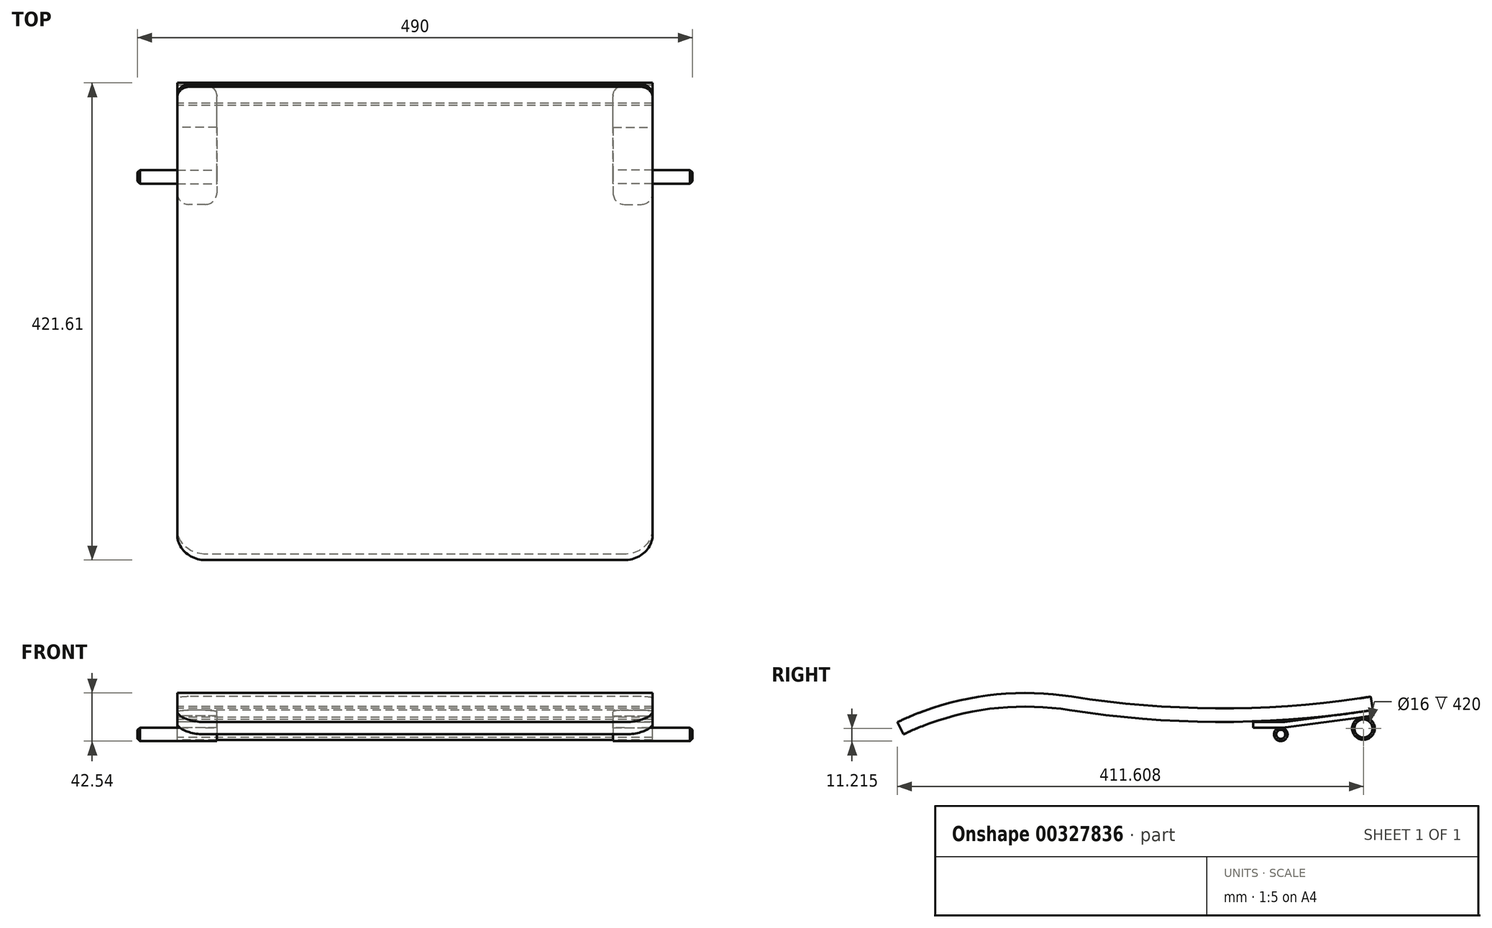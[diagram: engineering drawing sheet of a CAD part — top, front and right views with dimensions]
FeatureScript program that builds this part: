
annotation { "Feature Type Name" : "Feature", "Feature Type Description" : "" }
export const myFeature = defineFeature(function(context is Context, id is Id, definition is map)
    precondition{}
    {
        {
            var Q0;
            Q0=qCreatedBy(makeId("Right.planeOp"),FACE);
            var sketch = newSketch(context, id + "F0", { "sketchPlane" : qUnion([Q0])});
            skArc(sketch, "E0", {"start": v(-227.52, 21.5) * mm, "mid": v(-302.58, 21.9) * mm, "end": v(-374.38, 0) * mm});
            skArc(sketch, "E1", {"start": v(-227.52, 21.5) * mm, "mid": v(-93.54, 11.02) * mm, "end": v(40.43, 21.5) * mm});
            skArc(sketch, "E2.0", {"start": v(-225.65, 33.35) * mm, "mid": v(-304.32, 33.77) * mm, "end": v(-379.57, 10.82) * mm});
            skArc(sketch, "E2.1", {"start": v(-225.65, 33.35) * mm, "mid": v(-93.54, 23.02) * mm, "end": v(38.57, 33.35) * mm});
            skLineSegment(sketch, "E3", {"start": v(-379.57, 10.82) * mm, "end": v(-374.38, 0) * mm});
            skLineSegment(sketch, "E4", {"start": v(40.43, 21.5) * mm, "end": v(38.57, 33.35) * mm});
            skLineSegment(sketch, "E5", {"start": v(38.57, 33.35) * mm, "end": v(38.57, 33.35) * mm});
            skLineSegment(sketch, "E6", {"start": v(40.43, 21.5) * mm, "end": v(40.43, 21.5) * mm});
            skSolve(sketch);
        }
        {
            var Q0;
            Q0 = qSketchRegion(id + "F0", true);
            extrude(context, id + "F1", {"entities" : qUnion([Q0]), "endBound" : BoundingType.SYMMETRIC, "depth" : 420 * mm});
        }
        {
            var Q0;
            Q0=qCreatedBy(makeId("Right.planeOp"),FACE);
            var sketch = newSketch(context, id + "F2", { "sketchPlane" : qUnion([Q0])});
            skArc(sketch, "E7.0", {"start": v(-227.52, 21.5) * mm, "mid": v(-93.54, 11.02) * mm, "end": v(40.43, 21.5) * mm});
            skLineSegment(sketch, "E8", {"start": v(-65.33, 11) * mm, "end": v(-65.33, 6) * mm});
            skLineSegment(sketch, "E9", {"start": v(-65.33, 6) * mm, "end": v(-37.7, 6) * mm});
            skLineSegment(sketch, "E10", {"start": v(-36.77, 6.06) * mm, "end": v(40.62, 16.46) * mm});
            skLineSegment(sketch, "E11", {"start": v(40.62, 16.46) * mm, "end": v(39.95, 21.41) * mm});
            skLineSegment(sketch, "E12.0", {"start": v(-37.43, 11.02) * mm, "end": v(39.95, 21.41) * mm});
            skLineSegment(sketch, "E12.1", {"start": v(-65.33, 11) * mm, "end": v(-37.7, 11) * mm});
            skCircle(sketch, "E13", {"center": v(-40.94, 0) * mm, "radius": 6 * mm});
            skPoint(sketch, "E14.visualSharp", {"position": v(-37.57, 11) * mm});
            skArc(sketch, "E14.filletArc", {"start": v(-37.7, 11) * mm, "mid": v(-37.57, 11) * mm, "end": v(-37.43, 11.02) * mm});
            skPoint(sketch, "E15.visualSharp", {"position": v(-37.23, 6) * mm});
            skArc(sketch, "E15.filletArc", {"start": v(-37.7, 6) * mm, "mid": v(-37.23, 6.02) * mm, "end": v(-36.77, 6.06) * mm});
            skSolve(sketch);
        }
        {
            var Q0;
            Q0=makeQuery(id+"F1.opExtrude","CAP_EDGE",EDGE,{"disambiguationData":[OSD([sQuery(id+"F0.wireOp",EDGE,"E3")])],"isStart":false});
            var Q1;
            Q1=makeQuery(id+"F1.opExtrude","CAP_EDGE",EDGE,{"disambiguationData":[OSD([sQuery(id+"F0.wireOp",EDGE,"E3")])],"isStart":true});
            fillet(context, id + "F3", {"entities" : qUnion([Q0, Q1]), "radius" : 25 * mm, "tangentPropagation" : true, "allowEdgeOverflow" : false});
        }
        {
            var Q0;
            Q0=makeQuery(id+"F1.opExtrude","CAP_EDGE",EDGE,{"disambiguationData":[OSD([sQuery(id+"F0.wireOp",EDGE,"E4")])],"isStart":false});
            var Q1;
            Q1=makeQuery(id+"F1.opExtrude","CAP_EDGE",EDGE,{"disambiguationData":[OSD([sQuery(id+"F0.wireOp",EDGE,"E4")])],"isStart":true});
            fillet(context, id + "F4", {"entities" : qUnion([Q0, Q1]), "radius" : 10 * mm, "tangentPropagation" : true, "allowEdgeOverflow" : false});
        }
        {
            var Q0;
            Q0=qCreatedBy(makeId("Right.planeOp"),FACE);
            var sketch = newSketch(context, id + "F5", { "sketchPlane" : qUnion([Q0])});
            skCircle(sketch, "E16", {"center": v(32.04, 5.22) * mm, "radius": 10 * mm});
            skCircle(sketch, "E17", {"center": v(32.04, 5.22) * mm, "radius": 8 * mm});
            skSolve(sketch);
        }
        {
            var Q0;
            Q0=makeQuery(id+"F5.imprint","IMPRINT",FACE,{"disambiguationData":[TD([[makeQuery(id+"F5.imprint","IMPRINT",EDGE,{"derivedFrom":sQuery(id+"F5.wireOp",EDGE,"E16")}),1.0]])]});
            var Q1;
            Q1=makeQuery(id+"FTDRgdQHSnS7fxQ_1.opExtrude","CAP_FACE",FACE,{"disambiguationData":[OSD([sQuery(id+"FFSUCwoas4lt323_1.wireOp",EDGE,"86147a53-e2fd-4186-82ed-e5d5ec7286ad.0.0"),sQuery(id+"FFSUCwoas4lt323_1.wireOp",EDGE,"86147a53-e2fd-4186-82ed-e5d5ec7286ad.0.1"),sQuery(id+"FFSUCwoas4lt323_1.wireOp",EDGE,"86147a53-e2fd-4186-82ed-e5d5ec7286ad.0.2"),sQuery(id+"FFSUCwoas4lt323_1.wireOp",EDGE,"86147a53-e2fd-4186-82ed-e5d5ec7286ad.0.3"),sQuery(id+"FFSUCwoas4lt323_1.wireOp",EDGE,"86147a53-e2fd-4186-82ed-e5d5ec7286ad.0.4"),sQuery(id+"FFSUCwoas4lt323_1.wireOp",EDGE,"86147a53-e2fd-4186-82ed-e5d5ec7286ad.0.5"),sQuery(id+"FFSUCwoas4lt323_1.wireOp",EDGE,"86147a53-e2fd-4186-82ed-e5d5ec7286ad.0.6")])],"isStart":true});
            extrude(context, id + "F6", {"entities" : qUnion([Q0]), "endBound" : BoundingType.SYMMETRIC, "depth" : 420 * mm, "hasSecondDirection" : true, "secondDirectionBound" : SecondDirectionBoundingType.UP_TO_SURFACE, "secondDirectionOppositeDirection" : true, "secondDirectionBoundEntityFace" : qUnion([Q1]), "secondDirectionDepth" : 25 * mm});
        }
        {
            var Q0;
            Q0=makeQuery(id+"F1.opExtrude","CAP_FACE",FACE,{"disambiguationData":[OSD([sQuery(id+"F0.wireOp",EDGE,"E0"),sQuery(id+"F0.wireOp",EDGE,"E1"),sQuery(id+"F0.wireOp",EDGE,"E2.0"),sQuery(id+"F0.wireOp",EDGE,"E2.1"),sQuery(id+"F0.wireOp",EDGE,"E3"),sQuery(id+"F0.wireOp",EDGE,"E4")])],"isStart":false});
            var sketch = newSketch(context, id + "F7", { "sketchPlane" : qUnion([Q0])});
            skLineSegment(sketch, "E18.0.0", {"start": v(39.95, 21.41) * mm, "end": v(39.53, 21.36) * mm});
            skArc(sketch, "E18.0.1", {"start": v(39.53, 21.36) * mm, "mid": v(21.22, 18.7) * mm, "end": v(2.86, 16.43) * mm});
            skLineSegment(sketch, "E18.0.2", {"start": v(2.86, 16.43) * mm, "end": v(-37.43, 11.02) * mm});
            skArc(sketch, "E18.0.3", {"start": v(-37.43, 11.02) * mm, "mid": v(-37.57, 11) * mm, "end": v(-37.7, 11) * mm});
            skLineSegment(sketch, "E18.0.4", {"start": v(-37.7, 11) * mm, "end": v(-65.33, 11) * mm});
            skLineSegment(sketch, "E18.0.5", {"start": v(-65.33, 11) * mm, "end": v(-65.33, 6) * mm});
            skLineSegment(sketch, "E18.0.6", {"start": v(-65.33, 6) * mm, "end": v(-40.94, 6) * mm});
            skLineSegment(sketch, "E18.0.7", {"start": v(-40.94, 6) * mm, "end": v(-37.7, 6) * mm});
            skArc(sketch, "E18.0.8", {"start": v(-37.7, 6) * mm, "mid": v(-37.23, 6.02) * mm, "end": v(-36.77, 6.06) * mm});
            skLineSegment(sketch, "E18.0.9", {"start": v(-36.77, 6.06) * mm, "end": v(40.62, 16.46) * mm});
            skLineSegment(sketch, "E18.0.10", {"start": v(40.62, 16.46) * mm, "end": v(39.95, 21.41) * mm});
            skCircle(sketch, "E18.1.0", {"center": v(-40.94, 0) * mm, "radius": 6 * mm});
            skSolve(sketch);
        }
        {
            var Q0;
            {var subQ0=sQuery(id+"F7.wireOp",EDGE,"E18.0.0");Q0=makeQuery(id+"F7.imprint","IMPRINT",FACE,{"disambiguationData":[TD([[makeQuery(id+"F7.imprint","IMPRINT",EDGE,{"derivedFrom":subQ0}),1.0]])]});}
            extrude(context, id + "F8", {"entities" : qUnion([Q0]), "oppositeDirection" : true, "depth" : 35 * mm});
        }
        {
            var Q0;
            Q0=makeQuery(id+"F8.opExtrude","CAP_EDGE",EDGE,{"disambiguationData":[OSD([sQuery(id+"F7.wireOp",EDGE,"E18.0.5")])],"isStart":true});
            var Q1;
            Q1=makeQuery(id+"F8.opExtrude","CAP_EDGE",EDGE,{"disambiguationData":[OSD([sQuery(id+"F7.wireOp",EDGE,"E18.0.5")])],"isStart":false});
            var Q2;
            Q2=makeQuery(id+"F8.opExtrude","CAP_EDGE",EDGE,{"disambiguationData":[OSD([sQuery(id+"F7.wireOp",EDGE,"E18.0.10")])],"isStart":true});
            var Q3;
            Q3=makeQuery(id+"F8.opExtrude","CAP_EDGE",EDGE,{"disambiguationData":[OSD([sQuery(id+"F7.wireOp",EDGE,"E18.0.10")])],"isStart":false});
            fillet(context, id + "F9", {"entities" : qUnion([Q0, Q1, Q2, Q3]), "radius" : 10 * mm, "tangentPropagation" : true, "allowEdgeOverflow" : false});
        }
        {
            var Q0;
            Q0=makeQuery(id+"F7.imprint","IMPRINT",FACE,{"disambiguationData":[TD([[makeQuery(id+"F7.imprint","IMPRINT",EDGE,{"derivedFrom":sQuery(id+"F7.wireOp",EDGE,"E18.1.0")}),1.0]])]});
            extrude(context, id + "F10", {"entities" : qUnion([Q0]), "operationType" : NewBodyOperationType.ADD, "endBound" : BoundingType.SYMMETRIC, "depth" : 70 * mm});
        }
        {
            var Q0;
            Q0=makeQuery(id+"F10.opExtrude","CAP_FACE",FACE,{"disambiguationData":[OSD([sQuery(id+"F7.wireOp",EDGE,"E18.1.0")])],"isStart":false});
            chamfer(context, id + "F11", {"entities" : qUnion([Q0]), "width" : 2 * mm, "tangentPropagation" : true});
        }
        {
            var Q0;
            Q0=makeQuery(id+"F8.opExtrude","SWEPT_BODY",BODY,{"disambiguationData":[OSD([sQuery(id+"F7.wireOp",EDGE,"E18.0.0"),sQuery(id+"F7.wireOp",EDGE,"E18.0.1"),sQuery(id+"F7.wireOp",EDGE,"E18.0.2"),sQuery(id+"F7.wireOp",EDGE,"E18.0.3"),sQuery(id+"F7.wireOp",EDGE,"E18.0.4"),sQuery(id+"F7.wireOp",EDGE,"E18.0.5"),sQuery(id+"F7.wireOp",EDGE,"E18.0.6"),sQuery(id+"F7.wireOp",EDGE,"E18.0.7"),sQuery(id+"F7.wireOp",EDGE,"E18.0.8"),sQuery(id+"F7.wireOp",EDGE,"E18.0.9"),sQuery(id+"F7.wireOp",EDGE,"E18.0.10")])]});
            var Q1;
            Q1=makeQuery(id+"F10.opExtrude","SWEPT_BODY",BODY,{"disambiguationData":[OSD([sQuery(id+"F7.wireOp",EDGE,"E18.1.0")])]});
            var Q2;
            Q2=qCreatedBy(makeId("Right.planeOp"),FACE);
            mirror(context, id + "F12", {"entities" : qUnion([Q0, Q1]), "mirrorPlane" : qUnion([Q2])});
        }
    });
